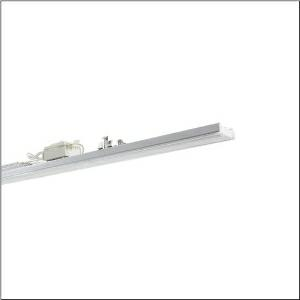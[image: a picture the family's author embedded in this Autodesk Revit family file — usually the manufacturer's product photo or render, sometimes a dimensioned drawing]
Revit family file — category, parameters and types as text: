
# Revit family: licross_11_recessed_mo_51te11dv4fxg
name_source: partatom
category: Lighting Fixtures
units: mm (PartAtom-declared; Revit-internal decimal feet)

## family parameters
Cut with Voids When Loaded = No
Host = Face
Light Source = No
Part Type = Normal
Room Calculation Point = No
Round Connector Dimension = Use Diameter
Shared = No

## types (1)
- --- (1 x LED, 15120 lm, 84.1 W, 4000K)
    Apparent Load = 84 VA
    CIE Flux Codes = 89 96 99 100 100
    Color Rendering = 80
    Color Temperature = 4000K
    Default Elevation = 1800 mm
    Description = Licross 11 Recessed MO, luminaire insert, of sheet steel, galvanised, coil coated, white, length: 2.250mm, width: 66mm, height: 67mm, LED rated luminous flux: 15.120lm, light colour: 840, SDCM (Standard Deviation of Colour Matching)MacAdam ≤ 2 SDCM (initial), control gear: DALI 2, with plug, 5-pole, with phase selection, mains connection: 220..240V, AC, 50/60Hz, rated input power: 84W, internal wiring halogen-free, primary light control with lens, of plastic, primary optical cover: cover, of PMMA, light emission: direct distribution, primary light characteristic: symmetric, protection rating (complete): IP54, insulation class (complete): insulation class I (protective earthing), certification: CE, ENEC, VDE, UKCA, protection symbol: D if used in an environment with non-conductive dust loads with corresponding accessories, impact resistance: IK06, permissible ambient temperature for indoor applications: -25..+35°C, corresponds to IFS (International Featured Standards) requirements for safety and quality in the food industry, reducing of maximum allowable ambient temperature of 5°C with ceiling mounting, LABS conformity tested according to VDMA 24364:2018-05, The light source and the operating device comply with the requirements of the Ecodesign Regulation (EU) 2019/2020 and are replaceable in accordance with this regulation, packaging unit: 1 piece
    Height = 58 mm
    Lamp = 1 x LED
    Lamp Light Flux = 15120 lm
    Lamp Power = 84.1 W
    Lamp count = 1
    Length = 2250 mm
    Luminous efficacy = 180 lm/W
    Manufacturer = Siteco
    ModVariant = No
    Model = 51TE11DV4FXG
    Mounting Place = Ceiling
    Mounting Type = Pendant
    Number of Poles = 1
    OnlyDefault = Yes
    Power Factor = 1
    Product Name = Licross 11 Recessed MO
    Product group = luminaire insert | ceiling pendant
    ProductGroupID = 901
    Protection Class = Protection class I
    Protection Degree = IP 54
    RLX_Detail_Level = 1
    RLX_Emergency_Light_Flux = 0 lm
    RLX_Emergency_Type = 0
    RLX_Emergency_Type_DB = No
    RlxData = <blob elided: 29649 chars, md5=85e13a94>
    Socket = socket
    Standby Power = 0 W
    System Light Flux = 15120 lm
    System Power = 84 W
    Type Comments = factory setting: luminous flux: 100 % | dim-lin: 254 | 378 mA
    Type Image = l_1296930.jpg
    URL = http://relux.com
    VarID = @adj_100153
    Voltage = 0 V
    Weight = 0.00 kg
    Width = 66 mm

## geometry (parser evidence)
native form markers: Blend x4, Sweep x9
no freeform markers — native parametric forms only
